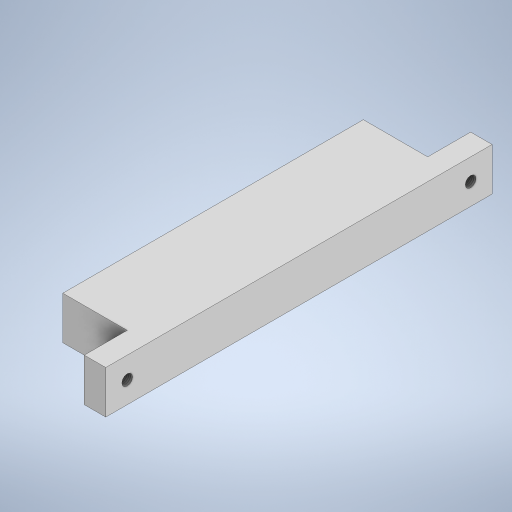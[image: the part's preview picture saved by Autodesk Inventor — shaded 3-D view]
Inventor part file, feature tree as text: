
AUTODESK INVENTOR PART (.ipt)
format: ipt  version: 2023 (Build 270158000, 158)  size: 274,432 bytes
history: native  units: mm
features: thread x4, extrude x3, other x1, sketch x1
ambient origin geometry x8: Origin, YZ Plane, XZ Plane, XY Plane, X Axis, Y Axis, Z Axis, Center Point
bodies: Body1 (feature_tree)
feature tree (9):
  other  "Твердое тело1"
  extrude  "Выдавливание1"  Depth=10.0mm
  extrude  "Выдавливание2"  Depth=20.0mm
  thread  "Резьба4"
  extrude  "Выдавливание3"  Depth=30.0mm
  thread  "Резьба7"
  thread  "Резьба8"
  thread  "Резьба9"
  sketch  "Эскиз3"
